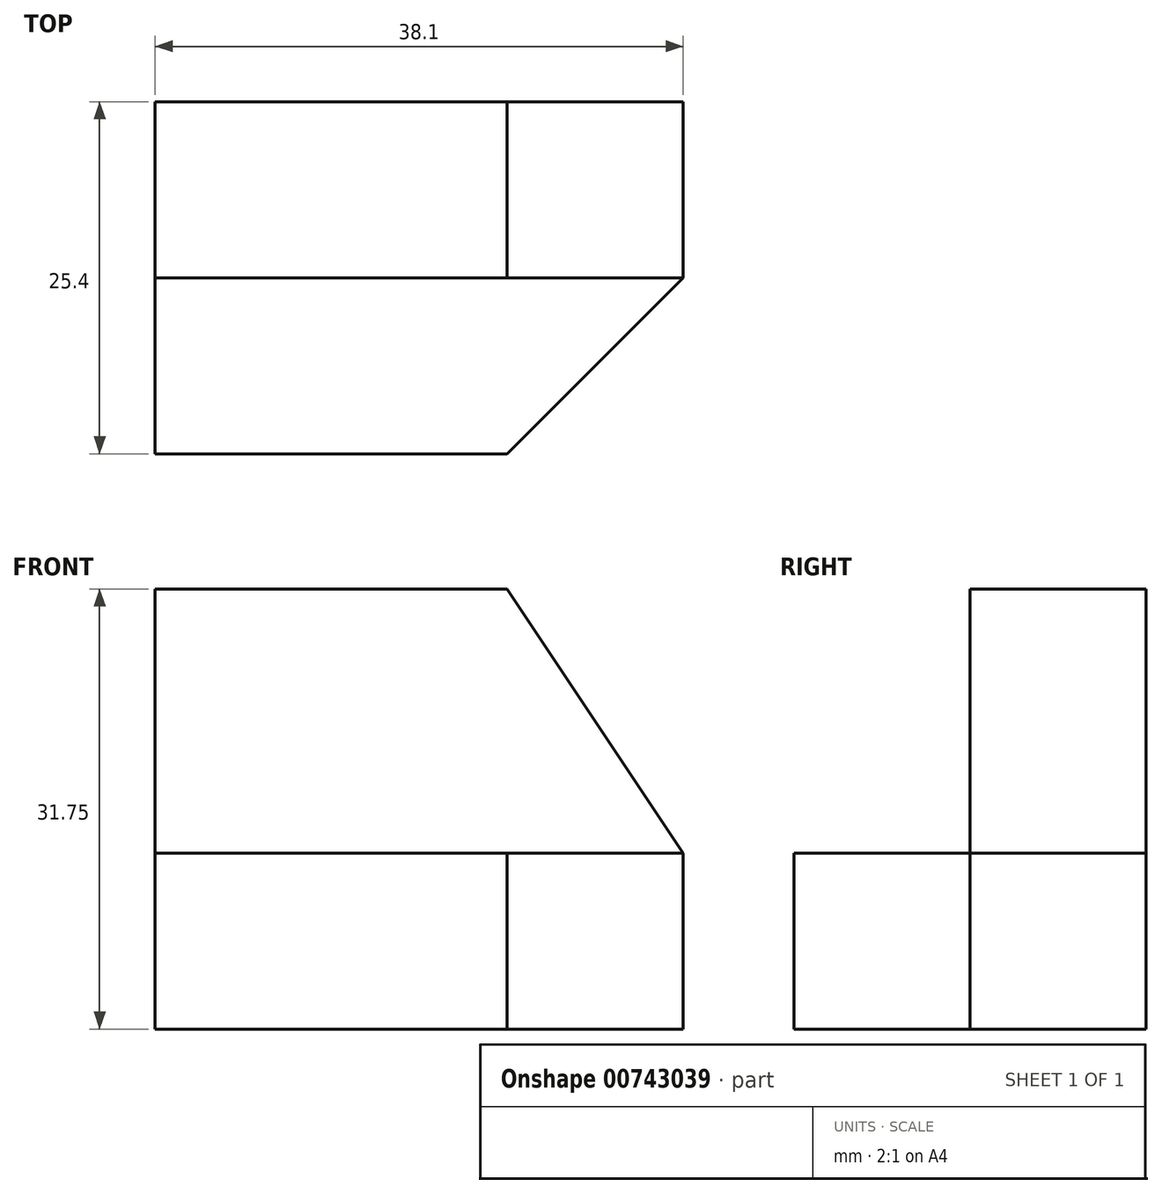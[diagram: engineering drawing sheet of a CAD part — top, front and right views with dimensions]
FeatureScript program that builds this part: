
annotation { "Feature Type Name" : "Feature", "Feature Type Description" : "" }
export const myFeature = defineFeature(function(context is Context, id is Id, definition is map)
    precondition{}
    {
        {
            var Q0;
            Q0=qCreatedBy(makeId("Front.planeOp"),FACE);
            var sketch = newSketch(context, id + "F0", { "sketchPlane" : qUnion([Q0])});
            skLineSegment(sketch, "E0", {"start": v(0, 0) * mm, "end": v(38.1, 0) * mm});
            skLineSegment(sketch, "E1", {"start": v(38.1, 0) * mm, "end": v(38.1, 31.75) * mm});
            skLineSegment(sketch, "E2", {"start": v(38.1, 31.75) * mm, "end": v(0, 31.75) * mm});
            skLineSegment(sketch, "E3", {"start": v(0, 31.75) * mm, "end": v(0, 0) * mm});
            skSolve(sketch);
        }
        {
            var Q0;
            Q0=makeQuery(id+"F0.imprint","IMPRINT",FACE,{"disambiguationData":[TD([[makeQuery(id+"F0.imprint","IMPRINT",EDGE,{"derivedFrom":sQuery(id+"F0.wireOp",EDGE,"E0")}),1.0]])]});
            extrude(context, id + "F1", {"entities" : qUnion([Q0]), "depth" : 25.4 * mm, "offsetDistance" : 25.4 * mm});
        }
        {
            var Q0;
            Q0=makeQuery(id+"F1.opExtrude","SWEPT_FACE",FACE,{"disambiguationData":[OSD([sQuery(id+"F0.wireOp",EDGE,"E3")])]});
            var sketch = newSketch(context, id + "F2", { "sketchPlane" : qUnion([Q0])});
            skLineSegment(sketch, "E4", {"start": v(12.7, 31.75) * mm, "end": v(12.7, 12.7) * mm});
            skLineSegment(sketch, "E5", {"start": v(12.7, 12.7) * mm, "end": v(25.4, 12.7) * mm});
            skSolve(sketch);
        }
        {
            var Q0;
            {var subQ0=sQuery(id+"F2.wireOp",EDGE,"E4");Q0=makeQuery(id+"F2.imprint","IMPRINT",FACE,{"disambiguationData":[TD([[makeQuery(id+"F2.imprint","IMPRINT",EDGE,{"derivedFrom":subQ0}),1.0]])]});}
            extrude(context, id + "F3", {"entities" : qUnion([Q0]), "operationType" : NewBodyOperationType.REMOVE, "depth" : 25.4 * mm, "offsetDistance" : 25.4 * mm, "hasSecondDirection" : true, "secondDirectionOppositeDirection" : true, "secondDirectionDepth" : 25.4 * mm});
        }
        {
            var Q0;
            Q0=makeQuery(id+"F1.opExtrude","CAP_FACE",FACE,{"disambiguationData":[OSD([sQuery(id+"F0.wireOp",EDGE,"E0"),sQuery(id+"F0.wireOp",EDGE,"E1"),sQuery(id+"F0.wireOp",EDGE,"E2"),sQuery(id+"F0.wireOp",EDGE,"E3")])],"isStart":true});
            var sketch = newSketch(context, id + "F4", { "sketchPlane" : qUnion([Q0])});
            skLineSegment(sketch, "E6", {"start": v(-25.4, 31.75) * mm, "end": v(-38.1, 12.7) * mm});
            skSolve(sketch);
        }
        {
            var Q0;
            {var subQ0=sQuery(id+"F4.wireOp",EDGE,"E6");Q0=makeQuery(id+"F4.imprint","IMPRINT",FACE,{"disambiguationData":[TD([[makeQuery(id+"F4.imprint","IMPRINT",EDGE,{"derivedFrom":subQ0}),-1.0]])]});}
            extrude(context, id + "F5", {"entities" : qUnion([Q0]), "operationType" : NewBodyOperationType.REMOVE, "oppositeDirection" : true, "depth" : 12.7 * mm, "offsetDistance" : 25.4 * mm});
        }
        {
            var Q0;
            Q0=makeQuery(id+"F1.opExtrude","SWEPT_FACE",FACE,{"disambiguationData":[OSD([sQuery(id+"F0.wireOp",EDGE,"E0")])]});
            var sketch = newSketch(context, id + "F6", { "sketchPlane" : qUnion([Q0])});
            skLineSegment(sketch, "E7", {"start": v(25.4, 25.4) * mm, "end": v(38.1, 12.7) * mm});
            skSolve(sketch);
        }
        {
            var Q0;
            {var subQ0=sQuery(id+"F6.wireOp",EDGE,"E7");Q0=makeQuery(id+"F6.imprint","IMPRINT",FACE,{"disambiguationData":[TD([[makeQuery(id+"F6.imprint","IMPRINT",EDGE,{"derivedFrom":subQ0}),1.0]])]});}
            extrude(context, id + "F7", {"entities" : qUnion([Q0]), "operationType" : NewBodyOperationType.REMOVE, "oppositeDirection" : true, "depth" : 12.7 * mm, "offsetDistance" : 25.4 * mm, "hasSecondDirection" : true, "secondDirectionOppositeDirection" : false, "secondDirectionDepth" : 25.4 * mm});
        }
        {
            var Q0;
            {var subQ1=sQuery(id+"F0.wireOp",EDGE,"E2");var subQ2=makeQuery(id+"F1.opExtrude","SWEPT_FACE",FACE,{"disambiguationData":[OSD([subQ1])]});var subQ3=sQuery(id+"F0.wireOp",EDGE,"E1");Q0=makeQuery(id+"F5.boolean.opBoolean","SPLIT",FACE,{"disambiguationData":[TD([makeQuery(id+"F1.opExtrude","SWEPT_FACE",FACE,{"disambiguationData":[OSD([subQ3])]})])],"derivedFrom":subQ2});}
            extrude(context, id + "F8", {"entities" : qUnion([Q0]), "operationType" : NewBodyOperationType.REMOVE, "oppositeDirection" : true, "depth" : 19.05 * mm, "offsetDistance" : 25.4 * mm});
        }
    });
